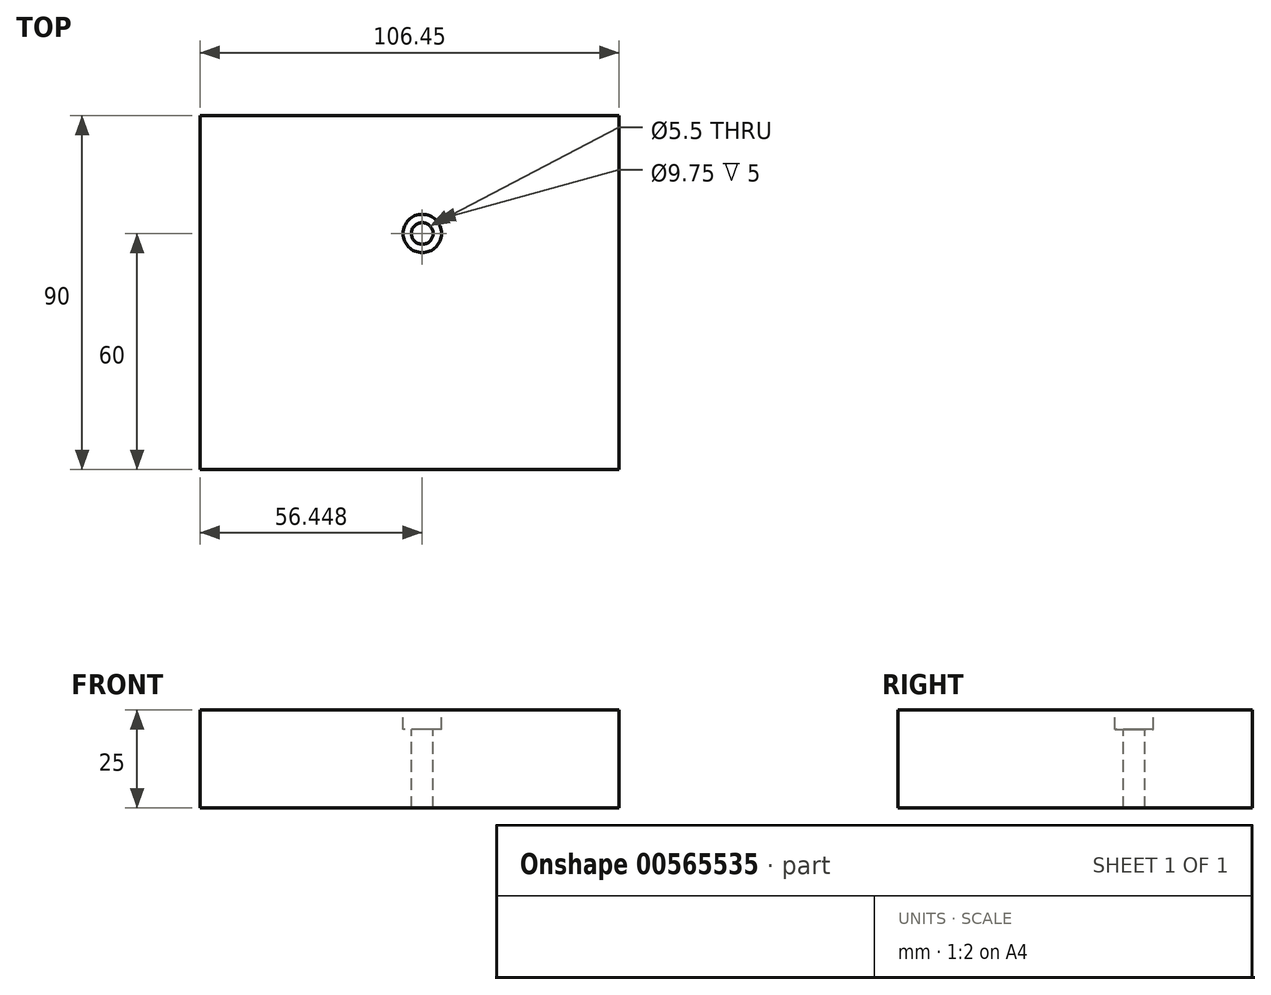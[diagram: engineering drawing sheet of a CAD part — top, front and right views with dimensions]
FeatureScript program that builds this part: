
annotation { "Feature Type Name" : "Feature", "Feature Type Description" : "" }
export const myFeature = defineFeature(function(context is Context, id is Id, definition is map)
    precondition{}
    {
        {
            var Q0;
            Q0=qCreatedBy(makeId("Top.planeOp"),FACE);
            var sketch = newSketch(context, id + "F0", { "sketchPlane" : qUnion([Q0])});
            skLineSegment(sketch, "E0.bottom", {"start": v(0, 0) * mm, "end": v(106.45, 0) * mm});
            skLineSegment(sketch, "E0.top", {"start": v(0, 90) * mm, "end": v(106.45, 90) * mm});
            skLineSegment(sketch, "E0.left", {"start": v(0, 0) * mm, "end": v(0, 90) * mm});
            skLineSegment(sketch, "E0.right", {"start": v(106.45, 0) * mm, "end": v(106.45, 90) * mm});
            skSolve(sketch);
        }
        {
            var Q0;
            Q0=makeQuery(id+"F0.imprint","IMPRINT",FACE,{"disambiguationData":[TD([[makeQuery(id+"F0.imprint","IMPRINT",EDGE,{"derivedFrom":sQuery(id+"F0.wireOp",EDGE,"E0.bottom")}),1.0]])]});
            var Q1;
            Q1=sQuery(id+"F0.wireOp",EDGE,"E0.top");
            var Q2;
            Q2=sQuery(id+"F0.wireOp",EDGE,"E0.left");
            var Q3;
            Q3=sQuery(id+"F0.wireOp",EDGE,"E0.bottom");
            var Q4;
            Q4=sQuery(id+"F0.wireOp",EDGE,"E0.right");
            extrude(context, id + "F1", {"entities" : qUnion([Q0]), "surfaceEntities" : qUnion([Q1, Q2, Q3, Q4]), "depth" : 25 * mm, "offsetDistance" : 25 * mm});
        }
        {
            var Q0;
            Q0=makeQuery(id+"F1.opExtrude","CAP_FACE",FACE,{"disambiguationData":[OSD([sQuery(id+"F0.wireOp",EDGE,"E0.bottom"),sQuery(id+"F0.wireOp",EDGE,"E0.top"),sQuery(id+"F0.wireOp",EDGE,"E0.left"),sQuery(id+"F0.wireOp",EDGE,"E0.right")])],"isStart":false});
            var sketch = newSketch(context, id + "F2", { "sketchPlane" : qUnion([Q0])});
            skPoint(sketch, "E1", {"position": v(56.45, 60) * mm});
            skSolve(sketch);
        }
        {
            var Q0;
            Q0=sQuery(id+"F2.wireOp",VERTEX,"E1");
            var Q1;
            Q1=makeQuery(id+"F1.opExtrude","SWEPT_BODY",BODY,{"disambiguationData":[OSD([sQuery(id+"F0.wireOp",EDGE,"E0.bottom"),sQuery(id+"F0.wireOp",EDGE,"E0.top"),sQuery(id+"F0.wireOp",EDGE,"E0.left"),sQuery(id+"F0.wireOp",EDGE,"E0.right")])]});
            hole(context, id + "F3", {"style" : HoleStyle.C_BORE, "endStyle" : HoleEndStyle.THROUGH, "standardTappedOrClearance" : lookupTablePath({ "standard" : "ISO", "fit" : "Normal", "size" : "M5", "type" : "Clearance" }), "standardBlindInLast" : lookupTablePath({ "fit" : "Standard", "standard" : "ISO", "size" : "M5", "type" : "Clearance" }), "holeDiameter" : 5.5 * mm, "cBoreDiameter" : 9.75 * mm, "cBoreDepth" : 5 * mm, "isTappedThrough" : true, "tappedDepth" : 12 * mm, "tapClearance" : 3, "locations" : qUnion([Q0]), "scope" : qUnion([Q1])});
        }
    });
